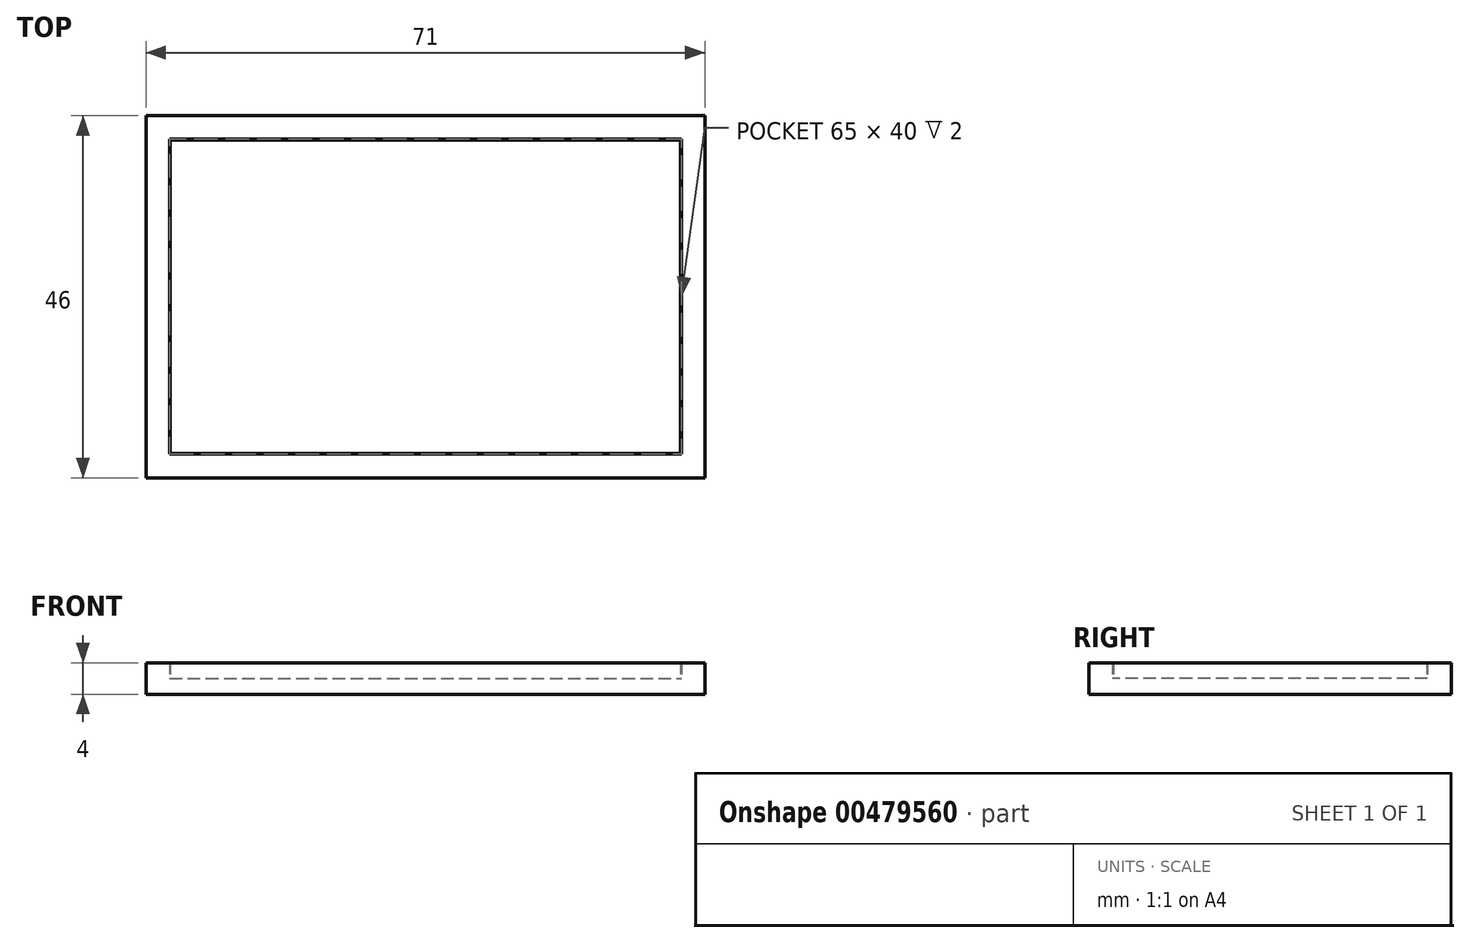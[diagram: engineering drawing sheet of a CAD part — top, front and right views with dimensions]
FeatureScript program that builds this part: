
annotation { "Feature Type Name" : "Feature", "Feature Type Description" : "" }
export const myFeature = defineFeature(function(context is Context, id is Id, definition is map)
    precondition{}
    {
        {
            var Q0;
            Q0=qCreatedBy(makeId("Top.planeOp"),FACE);
            var sketch = newSketch(context, id + "F0", { "sketchPlane" : qUnion([Q0])});
            skLineSegment(sketch, "E0.bottom", {"start": v(-32.5, 20) * mm, "end": v(32.5, 20) * mm});
            skLineSegment(sketch, "E0.top", {"start": v(-32.5, -20) * mm, "end": v(32.5, -20) * mm});
            skLineSegment(sketch, "E0.left", {"start": v(-32.5, 20) * mm, "end": v(-32.5, -20) * mm});
            skLineSegment(sketch, "E0.right", {"start": v(32.5, 20) * mm, "end": v(32.5, -20) * mm});
            skPoint(sketch, "E0.middle", {"position": v(0, 0) * mm});
            skLineSegment(sketch, "E1.0", {"start": v(-35.5, 23) * mm, "end": v(35.5, 23) * mm});
            skLineSegment(sketch, "E1.1", {"start": v(-35.5, 23) * mm, "end": v(-35.5, -23) * mm});
            skLineSegment(sketch, "E1.2", {"start": v(-35.5, -23) * mm, "end": v(35.5, -23) * mm});
            skLineSegment(sketch, "E1.3", {"start": v(35.5, 23) * mm, "end": v(35.5, -23) * mm});
            skLineSegment(sketch, "E2.0", {"start": v(-32.4, 19.9) * mm, "end": v(32.4, 19.9) * mm});
            skLineSegment(sketch, "E2.1", {"start": v(-32.4, 19.9) * mm, "end": v(-32.4, -19.9) * mm});
            skLineSegment(sketch, "E2.2", {"start": v(-32.4, -19.9) * mm, "end": v(32.4, -19.9) * mm});
            skLineSegment(sketch, "E2.3", {"start": v(32.4, 19.9) * mm, "end": v(32.4, -19.9) * mm});
            skSolve(sketch);
        }
        {
            var Q0;
            Q0=makeQuery(id+"F0.imprint","IMPRINT",FACE,{"disambiguationData":[TD([[makeQuery(id+"F0.imprint","IMPRINT",EDGE,{"derivedFrom":sQuery(id+"F0.wireOp",EDGE,"E2.0")}),-1.0]])]});
            extrude(context, id + "F1", {"entities" : qUnion([Q0]), "depth" : 2 * mm});
        }
        {
            var Q0;
            Q0=makeQuery(id+"F0.imprint","IMPRINT",FACE,{"disambiguationData":[TD([[makeQuery(id+"F0.imprint","IMPRINT",EDGE,{"derivedFrom":sQuery(id+"F0.wireOp",EDGE,"E2.0")}),-1.0]])]});
            var Q1;
            Q1=makeQuery(id+"F0.imprint","IMPRINT",FACE,{"disambiguationData":[TD([[makeQuery(id+"F0.imprint","IMPRINT",EDGE,{"derivedFrom":sQuery(id+"F0.wireOp",EDGE,"E0.bottom")}),-1.0]])]});
            var Q2;
            Q2=makeQuery(id+"F0.imprint","IMPRINT",FACE,{"disambiguationData":[TD([[makeQuery(id+"F0.imprint","IMPRINT",EDGE,{"derivedFrom":sQuery(id+"F0.wireOp",EDGE,"E0.bottom")}),1.0]])]});
            extrude(context, id + "F2", {"entities" : qUnion([Q0, Q1, Q2]), "oppositeDirection" : true, "depth" : 2 * mm});
        }
        {
            var Q0;
            Q0=makeQuery(id+"F0.imprint","IMPRINT",FACE,{"disambiguationData":[TD([[makeQuery(id+"F0.imprint","IMPRINT",EDGE,{"derivedFrom":sQuery(id+"F0.wireOp",EDGE,"E0.bottom")}),1.0]])]});
            extrude(context, id + "F3", {"entities" : qUnion([Q0]), "operationType" : NewBodyOperationType.ADD, "depth" : 2 * mm});
        }
    });
